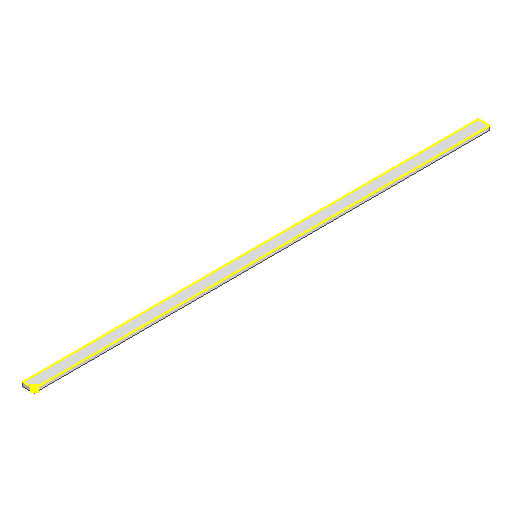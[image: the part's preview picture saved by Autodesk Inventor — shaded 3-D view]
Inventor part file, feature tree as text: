
AUTODESK INVENTOR PART (.ipt)
format: ipt  version: 2022 (Build 260153000, 153)  size: 84,992 bytes
history: native  units: mm
features: sketch x2, extrude x1, projected_geometry x1
ambient origin geometry x8: Origin, YZ Plane, XZ Plane, XY Plane, X Axis, Y Axis, Z Axis, Center Point
bodies: Solid1 (feature_tree)
feature tree (4):
  extrude  "Extrusion1"  Depth=200.0mm
  sketch  "Sketch2"  dims[d2=2.0mm d3=0.0mm]
  sketch  "Sketch1"  dims[d0=5.0mm d1=200.0mm]
  projected_geometry  "Projected Loop1"
